# Revit family: 902-0552
name_source: partatom
category: Generic Models
units: mm (PartAtom-declared; Revit-internal decimal feet)

## family parameters
Can host rebar = No
Cut with Voids When Loaded = No
Host = Face
Maintain Annotation Orientation = No
Part Type = Normal
Room Calculation Point = No
Round Connector Dimension = Use Diameter
Shared = No

## types (2) — shared parameters
AB_D1 = 13 mm  [stored 0.0426509 ft]
AB_D2 = 23 mm
AB_H1 = 22 mm  [stored 0.0721785 ft]
AB_H2 = 2 mm  [stored 0.00656168 ft]
C_H1 = 42 mm  [stored 0.137795 ft]
C_L1 = 125 mm  [stored 0.410105 ft]
C_L2 = 155 mm  [stored 0.50853 ft]
Default Elevation = 1219 mm
Focus_D1 = 31 mm  [stored 0.101706 ft]
Focus_D2 = 8 mm  [stored 0.0262467 ft]
Focus_L1 = 800 mm  [stored 2.62467 ft]
Focus_L2 = 400 mm  [stored 1.31234 ft]
Focus_R1 = 100 mm  [stored 0.328084 ft]
Focus_T1 = 24 mm  [stored 0.0787402 ft]
H_D1 = 420 mm  [stored 1.37795 ft]
H_H1 = 376 mm  [stored 1.2336 ft]
H_L1 = 120 mm  [stored 0.393701 ft]
H_L2 = 40 mm  [stored 0.131234 ft]
K_D1 = 5 mm  [stored 0.0164042 ft]
M_H1 = 50 mm  [stored 0.164042 ft]
M_L1 = 60 mm  [stored 0.19685 ft]
M_L2 = 240 mm  [stored 0.787402 ft]
Manufacturer = Prolicht
Model = 902-0552
R4 = 03 Crystal White
S1_H2 = 30 mm  [stored 0.0984252 ft]
S_D1 = 8 mm  [stored 0.0262467 ft]
S_D2 = 2 mm  [stored 0.00656168 ft]
S_H1 = 2 mm  [stored 0.00656168 ft]
Suspension height = 400 mm  [stored 1.31234 ft]

## per-type parameters (varying)
| type | Light_distribution |
| 20 | lvk_Focus_2023 : 20° |
| 40 | lvk_Focus_2023 : 40° |

note: [stored X ft] marks values corroborated as IEEE doubles in the binary element streams (Revit-internal decimal feet)

## geometry (parser evidence)
native form markers: Extrusion x1, Sweep x5
no freeform markers — native parametric forms only
